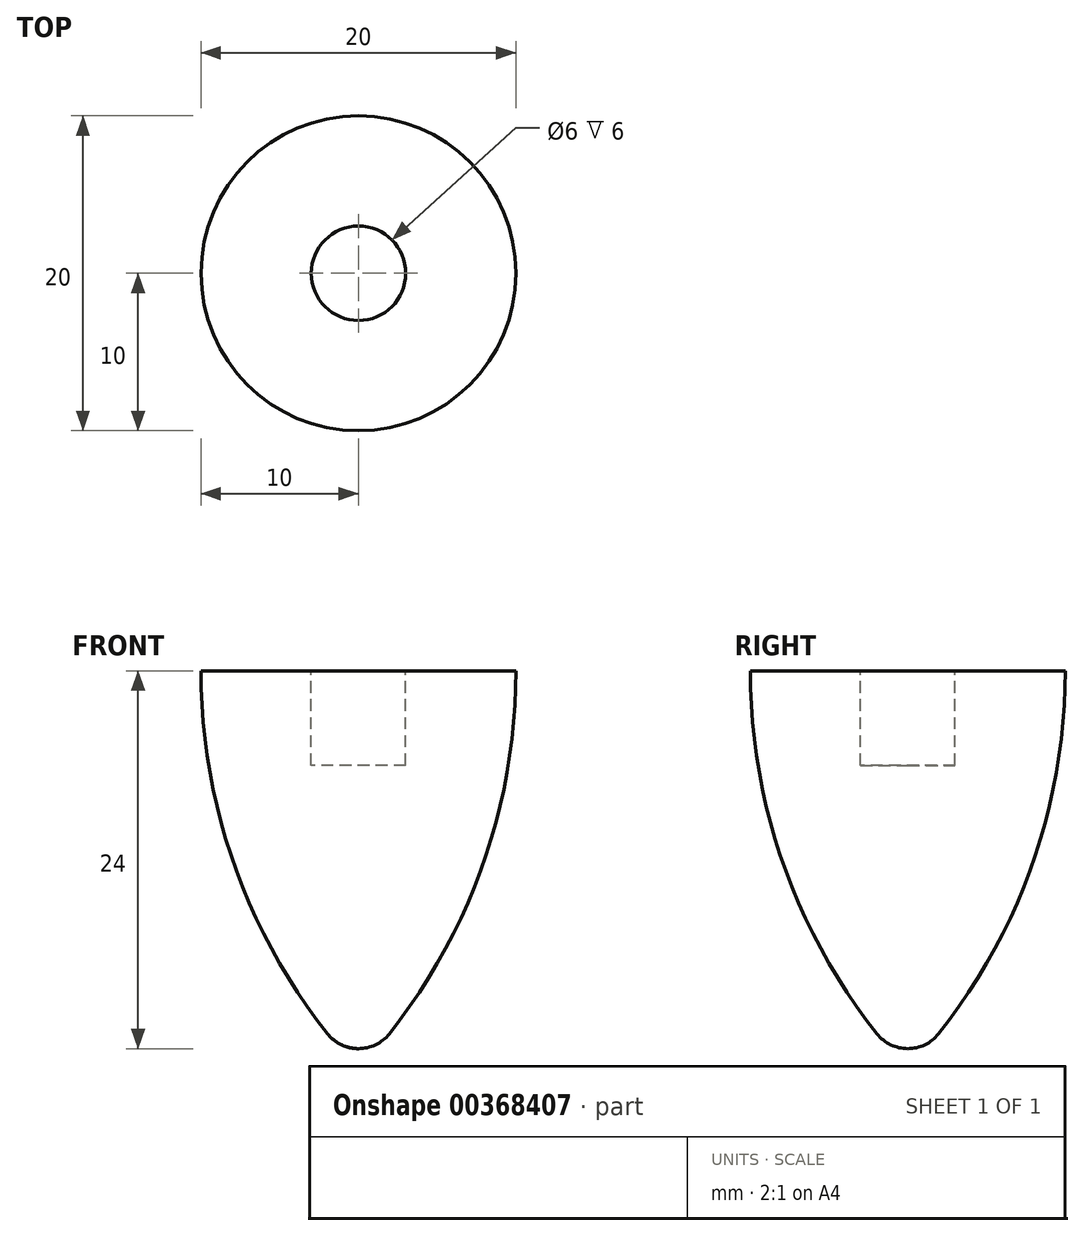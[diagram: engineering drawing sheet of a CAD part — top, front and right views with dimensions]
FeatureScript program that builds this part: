
annotation { "Feature Type Name" : "Feature", "Feature Type Description" : "" }
export const myFeature = defineFeature(function(context is Context, id is Id, definition is map)
    precondition{}
    {
        {
            var Q0;
            Q0=qCreatedBy(makeId("Front.planeOp"),FACE);
            var sketch = newSketch(context, id + "F0", { "sketchPlane" : qUnion([Q0])});
            skLineSegment(sketch, "E0", {"start": v(0, 0) * mm, "end": v(0, -24) * mm});
            skArc(sketch, "E1", {"start": v(0, -24) * mm, "mid": v(1.09, -23.75) * mm, "end": v(1.96, -23.05) * mm});
            skLineSegment(sketch, "E2", {"start": v(0, 0) * mm, "end": v(10, 0) * mm});
            skLineSegment(sketch, "E3", {"start": v(10, 0) * mm, "end": v(10, 2) * mm, "construction": true});
            skArc(sketch, "E4", {"start": v(1.96, -23.05) * mm, "mid": v(7.93, -12.2) * mm, "end": v(10, 0) * mm});
            skSolve(sketch);
        }
        {
            var Q0;
            Q0 = qSketchRegion(id + "F0", true);
            var Q1;
            Q1=sQuery(id+"F0.wireOp",EDGE,"E0");
            revolve(context, id + "F1", {"entities" : qUnion([Q0]), "axis" : qUnion([Q1]), "revolveType" : RevolveType.FULL});
        }
        {
            var Q0;
            Q0=makeQuery(id+"F1.opRevolve","SWEPT_FACE",FACE,{"disambiguationData":[OSD([sQuery(id+"F0.wireOp",EDGE,"E2")])]});
            var sketch = newSketch(context, id + "F2", { "sketchPlane" : qUnion([Q0])});
            skCircle(sketch, "E5", {"center": v(0, 0) * mm, "radius": 3 * mm});
            skSolve(sketch);
        }
        {
            var Q0;
            Q0 = qSketchRegion(id + "F2", true);
            extrude(context, id + "F3", {"entities" : qUnion([Q0]), "operationType" : NewBodyOperationType.REMOVE, "oppositeDirection" : true, "depth" : 6 * mm});
        }
    });
